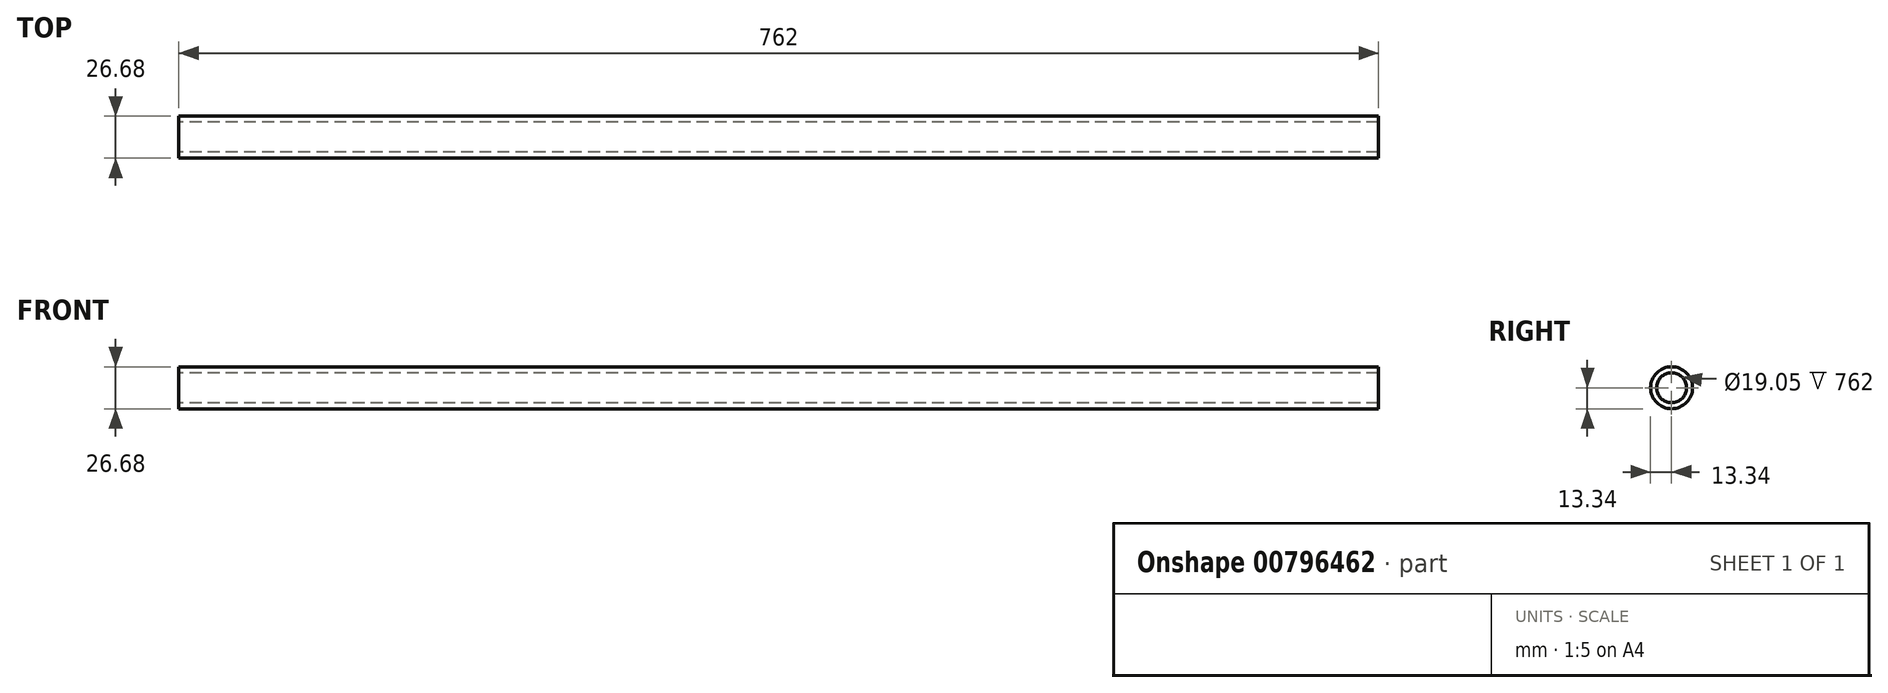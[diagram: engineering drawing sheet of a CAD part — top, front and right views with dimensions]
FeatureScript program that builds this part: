
annotation { "Feature Type Name" : "Feature", "Feature Type Description" : "" }
export const myFeature = defineFeature(function(context is Context, id is Id, definition is map)
    precondition{}
    {
        {
            var Q0;
            Q0=qCreatedBy(makeId("Right.planeOp"),FACE);
            var sketch = newSketch(context, id + "F0", { "sketchPlane" : qUnion([Q0])});
            skCircle(sketch, "E0", {"center": v(0, 0) * mm, "radius": 9.53 * mm});
            skCircle(sketch, "E1.0", {"center": v(0, 0) * mm, "radius": 13.33 * mm});
            skSolve(sketch);
        }
        {
            var Q0;
            Q0=qSketchRegion(id+"F0",true);
            extrude(context, id + "F1", {"entities" : qUnion([Q0]), "depth" : 762 * mm, "offsetDistance" : 25.4 * mm});
        }
    });
